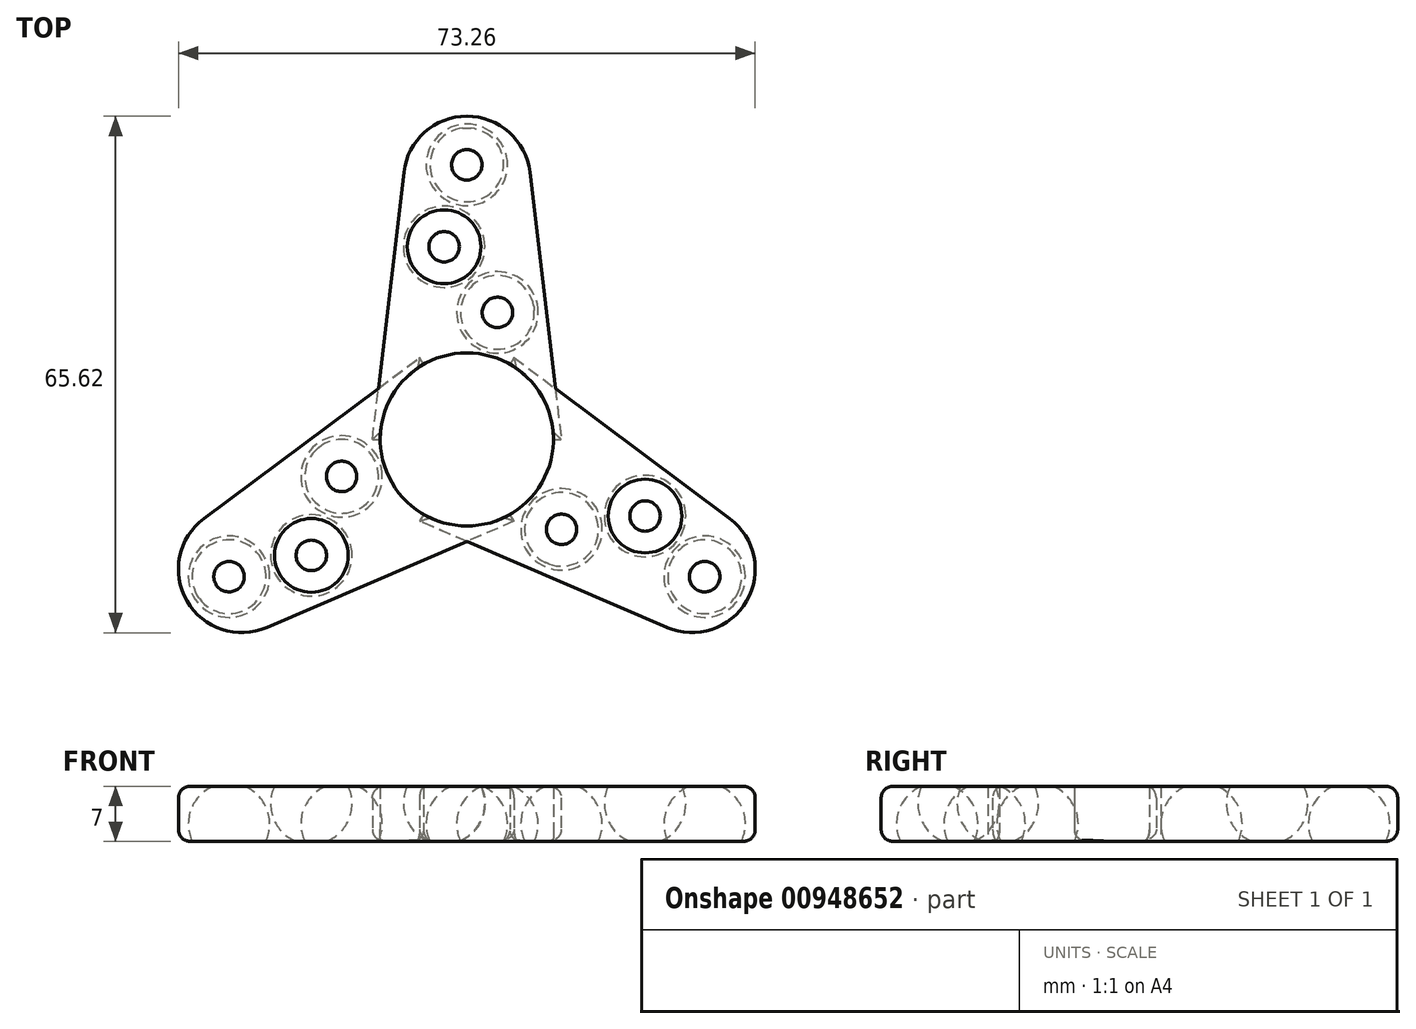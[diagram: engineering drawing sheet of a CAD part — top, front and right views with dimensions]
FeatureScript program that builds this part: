
annotation { "Feature Type Name" : "Feature", "Feature Type Description" : "" }
export const myFeature = defineFeature(function(context is Context, id is Id, definition is map)
    precondition{}
    {
        {
            var Q0;
            Q0=qCreatedBy(makeId("Top.planeOp"),FACE);
            var sketch = newSketch(context, id + "F0", { "sketchPlane" : qUnion([Q0])});
            skLineSegment(sketch, "E0", {"start": v(-12, 0) * mm, "end": v(-8, 33.94) * mm});
            skLineSegment(sketch, "E1", {"start": v(-8, 33.94) * mm, "end": v(8, 33.94) * mm});
            skLineSegment(sketch, "E2", {"start": v(8, 33.94) * mm, "end": v(12, 0) * mm});
            skArc(sketch, "E3", {"start": v(8, 33.94) * mm, "mid": v(0, 41.06) * mm, "end": v(-8, 33.94) * mm});
            skLineSegment(sketch, "E4", {"start": v(-12, 0) * mm, "end": v(12, 0) * mm});
            skCircle(sketch, "E5", {"center": v(0, 0) * mm, "radius": 11 * mm});
            skPoint(sketch, "E6", {"position": v(0, 34.88) * mm});
            skCircle(sketch, "E7", {"center": v(0, 34.88) * mm, "radius": 5.17 * mm});
            skPoint(sketch, "E8", {"position": v(-2.9, 24.48) * mm});
            skCircle(sketch, "E9", {"center": v(-2.9, 24.48) * mm, "radius": 5.17 * mm});
            skPoint(sketch, "E10", {"position": v(3.88, 16.13) * mm});
            skCircle(sketch, "E11", {"center": v(3.88, 16.13) * mm, "radius": 5.17 * mm});
            skLineSegment(sketch, "E12", {"start": v(-2.9, 24.48) * mm, "end": v(3.88, 16.13) * mm});
            skSolve(sketch);
        }
        {
            var Q0;
            Q0 = qSketchRegion(id + "F0", true);
            var Q1;
            Q1=makeQuery(id+"F0.imprint","IMPRINT",FACE,{"disambiguationData":[TD([[makeQuery(id+"F0.imprint","IMPRINT",EDGE,{"derivedFrom":sQuery(id+"F0.wireOp",EDGE,"E11")}),1.0]])]});
            var Q2;
            Q2=makeQuery(id+"F0.imprint","IMPRINT",FACE,{"disambiguationData":[TD([[makeQuery(id+"F0.imprint","IMPRINT",EDGE,{"derivedFrom":sQuery(id+"F0.wireOp",EDGE,"E9")}),1.0]])]});
            var Q3;
            {var subQ0=sQuery(id+"F0.wireOp",EDGE,"E7");var subQ1=sQuery(id+"F0.wireOp",EDGE,"E1");var subQ2=makeQuery(id+"F0.imprint","INTERSECT",VERTEX,{"disambiguationData":[OD(0.0)],"derivedFrom":[subQ1,subQ0]});Q3=makeQuery(id+"F0.imprint","IMPRINT",FACE,{"disambiguationData":[TD([[makeQuery(id+"F0.imprint","IMPRINT",EDGE,{"disambiguationData":[TD([[subQ2,-1.0]])],"derivedFrom":subQ1}),-1.0]])]});}
            var Q4;
            {var subQ0=sQuery(id+"F0.wireOp",EDGE,"E7");var subQ1=sQuery(id+"F0.wireOp",EDGE,"E1");var subQ2=makeQuery(id+"F0.imprint","INTERSECT",VERTEX,{"disambiguationData":[OD(0.0)],"derivedFrom":[subQ1,subQ0]});Q4=makeQuery(id+"F0.imprint","IMPRINT",FACE,{"disambiguationData":[TD([[makeQuery(id+"F0.imprint","IMPRINT",EDGE,{"disambiguationData":[TD([[subQ2,-1.0]])],"derivedFrom":subQ1}),1.0]])]});}
            extrude(context, id + "F1", {"entities" : qUnion([Q0, Q1, Q2, Q3, Q4]), "depth" : 7 * mm, "offsetDistance" : 25 * mm});
        }
        {
            var Q0;
            Q0=makeQuery(id+"F1.opExtrude","CAP_EDGE",EDGE,{"disambiguationData":[OSD([sQuery(id+"F0.wireOp",EDGE,"E2")])],"isStart":false});
            var Q1;
            Q1=makeQuery(id+"F1.opExtrude","CAP_FACE",FACE,{"disambiguationData":[OSD([sQuery(id+"F0.wireOp",EDGE,"E0"),sQuery(id+"F0.wireOp",EDGE,"E2"),sQuery(id+"F0.wireOp",EDGE,"E3"),sQuery(id+"F0.wireOp",EDGE,"E4"),sQuery(id+"F0.wireOp",EDGE,"E5")])],"isStart":true});
            fillet(context, id + "F2", {"entities" : qUnion([Q0, Q1]), "radius" : 1.5 * mm, "tangentPropagation" : true, "allowEdgeOverflow" : false});
        }
        {
            var Q0;
            Q0=makeQuery(id+"F1.opExtrude","SWEPT_FACE",FACE,{"disambiguationData":[OSD([sQuery(id+"F0.wireOp",EDGE,"E4")])]});
            var sketch = newSketch(context, id + "F3", { "sketchPlane" : qUnion([Q0])});
            skLineSegment(sketch, "E13.bottom", {"start": v(-20.3, 18.4) * mm, "end": v(18, 18.4) * mm});
            skLineSegment(sketch, "E13.top", {"start": v(-20.3, -8.7) * mm, "end": v(18, -8.7) * mm});
            skLineSegment(sketch, "E13.left", {"start": v(-20.3, 18.4) * mm, "end": v(-20.3, -8.7) * mm});
            skLineSegment(sketch, "E13.right", {"start": v(18, 18.4) * mm, "end": v(18, -8.7) * mm});
            skLineSegment(sketch, "E14", {"start": v(0, -8.7) * mm, "end": v(0, 18.4) * mm});
            skSolve(sketch);
        }
        {
            var Q0;
            Q0=sQuery(id+"F0.wireOp",EDGE,"E12");
            var Q1;
            Q1=qCreatedBy(makeId("Right.planeOp"),FACE);
            cPlane(context, id + "F4", {"entities" : qUnion([Q0, Q1]), "cplaneType" : CPlaneType.LINE_ANGLE, "offset" : 25 * mm, "angle" : 0 * degree, "width" : 150 * mm, "height" : 150 * mm});
        }
        {
            var Q0;
            Q0=qCreatedBy(id+"F4.planeOp",FACE);
            var sketch = newSketch(context, id + "F5", { "sketchPlane" : qUnion([Q0])});
            skPoint(sketch, "E15", {"position": v(-20.82, 4.8) * mm});
            skPoint(sketch, "E16", {"position": v(-10.08, 2.2) * mm});
            skCircle(sketch, "E17", {"center": v(-10.08, 2.2) * mm, "radius": 5.17 * mm});
            skCircle(sketch, "E18", {"center": v(-20.82, 4.8) * mm, "radius": 5.17 * mm});
            skLineSegment(sketch, "E19", {"start": v(-10.08, 2.2) * mm, "end": v(-10.08, 0) * mm});
            skLineSegment(sketch, "E20", {"start": v(-20.82, 4.8) * mm, "end": v(-20.82, 0) * mm});
            skLineSegment(sketch, "E21", {"start": v(-10.08, 2.2) * mm, "end": v(-10.08, 8.72) * mm});
            skLineSegment(sketch, "E22", {"start": v(-10.08, 8.72) * mm, "end": v(-10.08, -5.87) * mm});
            skLineSegment(sketch, "E23", {"start": v(-20.82, 0) * mm, "end": v(-20.82, 11.26) * mm});
            skLineSegment(sketch, "E24", {"start": v(-20.82, 11.26) * mm, "end": v(-20.82, -3.42) * mm});
            skSolve(sketch);
        }
        {
            var Q0;
            Q0=sQuery(id+"F0.wireOp",VERTEX,"E6");
            var Q1;
            Q1=qCreatedBy(makeId("Front.planeOp"),FACE);
            cPlane(context, id + "F6", {"entities" : qUnion([Q0, Q1]), "cplaneType" : CPlaneType.PLANE_POINT, "offset" : 25 * mm, "width" : 150 * mm, "height" : 150 * mm});
        }
        {
            var Q0;
            {var subQ0=sQuery(id+"F5.wireOp",EDGE,"E22");var subQ4=makeQuery(id+"F5.imprint","IMPRINT",VERTEX,{"derivedFrom":subQ0});Q0=makeQuery(id+"F5.imprint","IMPRINT",FACE,{"disambiguationData":[TD([[makeQuery(id+"F5.imprint","IMPRINT",EDGE,{"disambiguationData":[TD([[subQ4,1.0]])],"derivedFrom":subQ0}),1.0]])]});}
            var Q1;
            Q1=sQuery(id+"F5.wireOp",EDGE,"E22");
            revolve(context, id + "F7", {"operationType" : NewBodyOperationType.REMOVE, "surfaceOperationType" : NewSurfaceOperationType.NEW, "entities" : qUnion([Q0]), "axis" : qUnion([Q1]), "revolveType" : RevolveType.FULL, "oppositeDirection" : true});
        }
        {
            var Q0;
            {var subQ0=sQuery(id+"F5.wireOp",EDGE,"E24");var subQ5=makeQuery(id+"F5.imprint","IMPRINT",VERTEX,{"disambiguationData":[OD(0.0)],"derivedFrom":subQ0});Q0=makeQuery(id+"F5.imprint","IMPRINT",FACE,{"disambiguationData":[TD([[makeQuery(id+"F5.imprint","IMPRINT",EDGE,{"disambiguationData":[TD([[subQ5,-1.0]])],"derivedFrom":subQ0}),1.0]])]});}
            var Q1;
            Q1=sQuery(id+"F5.wireOp",EDGE,"E24");
            revolve(context, id + "F8", {"operationType" : NewBodyOperationType.REMOVE, "surfaceOperationType" : NewSurfaceOperationType.NEW, "entities" : qUnion([Q0]), "axis" : qUnion([Q1]), "revolveType" : RevolveType.FULL, "oppositeDirection" : true});
        }
        {
            var Q0;
            Q0=qCreatedBy(id+"F6.planeOp",FACE);
            var sketch = newSketch(context, id + "F9", { "sketchPlane" : qUnion([Q0])});
            skPoint(sketch, "E25", {"position": v(0, 0) * mm});
            skPoint(sketch, "E26", {"position": v(0, 2.2) * mm});
            skLineSegment(sketch, "E27", {"start": v(0, 0) * mm, "end": v(0, 2.2) * mm});
            skLineSegment(sketch, "E28", {"start": v(0, 12) * mm, "end": v(0, -9.58) * mm});
            skCircle(sketch, "E29", {"center": v(0, 2.2) * mm, "radius": 5.17 * mm});
            skSolve(sketch);
        }
        {
            var Q0;
            {var subQ0=sQuery(id+"F9.wireOp",EDGE,"E27");Q0=makeQuery(id+"F9.imprint","IMPRINT",FACE,{"disambiguationData":[TD([[makeQuery(id+"F9.imprint","IMPRINT",EDGE,{"derivedFrom":subQ0}),-1.0]])]});}
            var Q1;
            Q1=sQuery(id+"F9.wireOp",EDGE,"E28");
            revolve(context, id + "F10", {"operationType" : NewBodyOperationType.REMOVE, "surfaceOperationType" : NewSurfaceOperationType.NEW, "entities" : qUnion([Q0]), "axis" : qUnion([Q1]), "revolveType" : RevolveType.FULL, "oppositeDirection" : true});
        }
        {
            var Q0;
            Q0=makeQuery(id+"F1.opExtrude","SWEPT_BODY",BODY,{"disambiguationData":[OSD([sQuery(id+"F0.wireOp",EDGE,"E0"),sQuery(id+"F0.wireOp",EDGE,"E2"),sQuery(id+"F0.wireOp",EDGE,"E3"),sQuery(id+"F0.wireOp",EDGE,"E4")])]});
            var Q1;
            Q1=sQuery(id+"F3.wireOp",EDGE,"E14");
            transform(context, id + "F11", {"entities" : qUnion([Q0]), "transformType" : TransformType.ROTATION, "transformAxis" : qUnion([Q1]), "angle" : 120 * degree, "makeCopy" : true});
        }
        {
            var Q0;
            Q0=makeQuery(id+"F1.opExtrude","SWEPT_BODY",BODY,{"disambiguationData":[OSD([sQuery(id+"F0.wireOp",EDGE,"E0"),sQuery(id+"F0.wireOp",EDGE,"E2"),sQuery(id+"F0.wireOp",EDGE,"E3"),sQuery(id+"F0.wireOp",EDGE,"E4")])]});
            var Q1;
            Q1=sQuery(id+"F3.wireOp",EDGE,"E14");
            transform(context, id + "F12", {"entities" : qUnion([Q0]), "transformType" : TransformType.ROTATION, "transformAxis" : qUnion([Q1]), "angle" : 120 * degree, "oppositeDirection" : true, "makeCopy" : true});
        }
        {
            var Q0;
            {var subQ0=sQuery(id+"F0.wireOp",EDGE,"E5");var subQ1=sQuery(id+"F0.wireOp",EDGE,"E4");var subQ2=makeQuery(id+"F0.imprint","INTERSECT",VERTEX,{"disambiguationData":[OD(0.0)],"derivedFrom":[subQ1,subQ0]});Q0=makeQuery(id+"F0.imprint","IMPRINT",FACE,{"disambiguationData":[TD([[makeQuery(id+"F0.imprint","IMPRINT",EDGE,{"disambiguationData":[TD([[subQ2,-1.0]])],"derivedFrom":subQ1}),1.0]])]});}
            var Q1;
            {var subQ0=sQuery(id+"F0.wireOp",EDGE,"E5");var subQ1=sQuery(id+"F0.wireOp",EDGE,"E4");var subQ2=makeQuery(id+"F0.imprint","INTERSECT",VERTEX,{"disambiguationData":[OD(0.0)],"derivedFrom":[subQ1,subQ0]});Q1=makeQuery(id+"F0.imprint","IMPRINT",FACE,{"disambiguationData":[TD([[makeQuery(id+"F0.imprint","IMPRINT",EDGE,{"disambiguationData":[TD([[subQ2,-1.0]])],"derivedFrom":subQ1}),-1.0]])]});}
            extrude(context, id + "F13", {"entities" : qUnion([Q0, Q1]), "operationType" : NewBodyOperationType.REMOVE, "depth" : 25 * mm, "offsetDistance" : 25 * mm});
        }
    });
